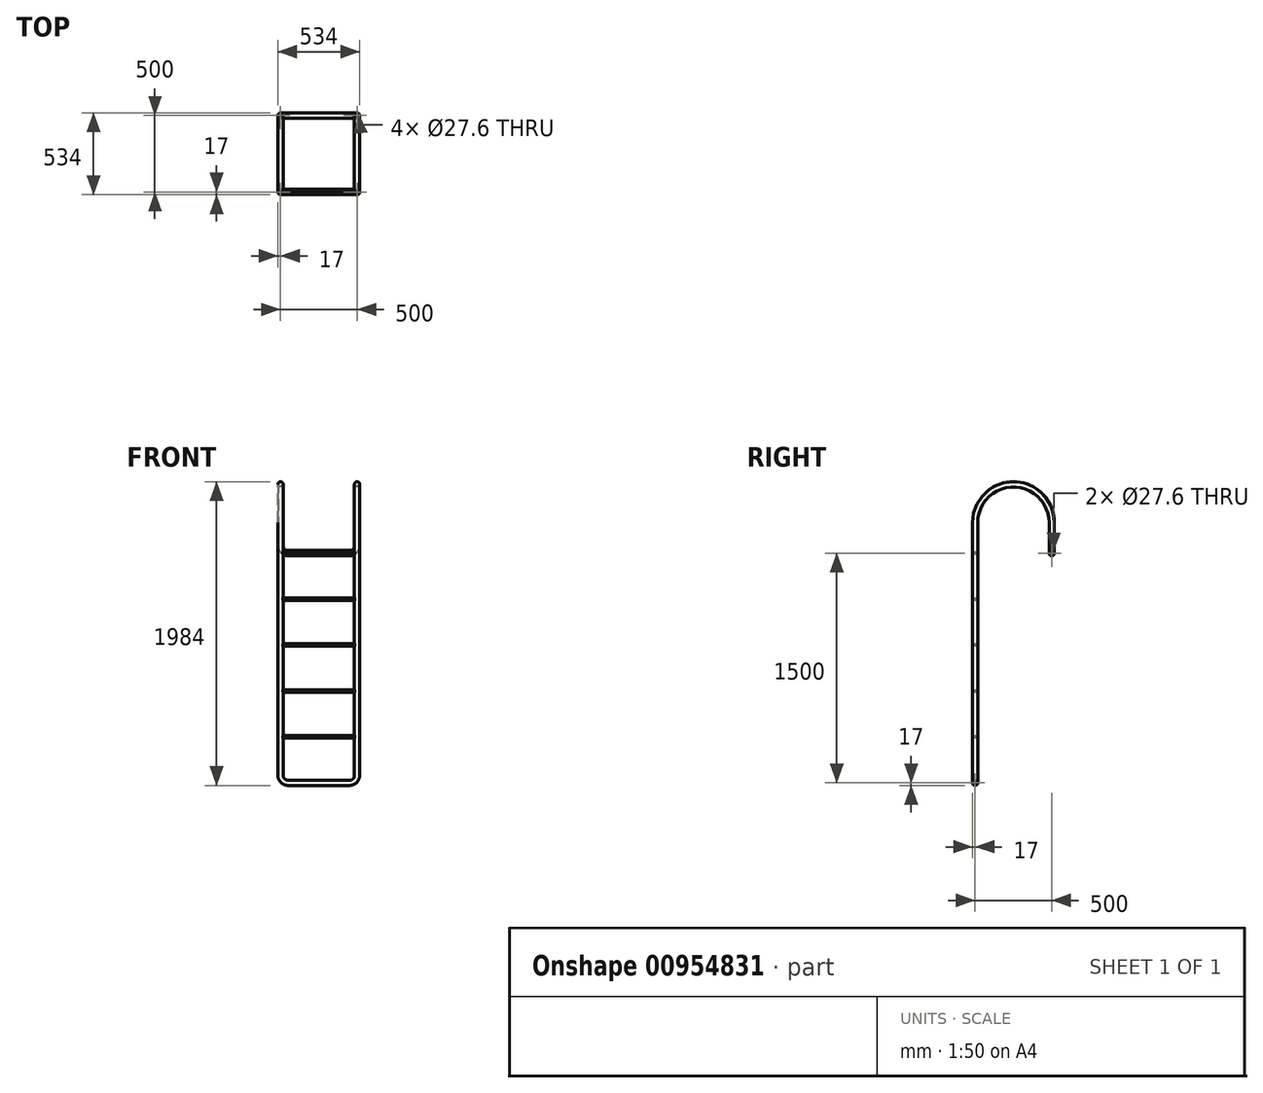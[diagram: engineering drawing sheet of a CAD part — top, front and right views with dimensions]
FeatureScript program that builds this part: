
annotation { "Feature Type Name" : "Feature", "Feature Type Description" : "" }
export const myFeature = defineFeature(function(context is Context, id is Id, definition is map)
    precondition{}
    {
        {
            var Q0;
            Q0=qCreatedBy(makeId("Right.planeOp"),FACE);
            cPlane(context, id + "F0", {"entities" : qUnion([Q0]), "cplaneType" : CPlaneType.OFFSET, "offset" : 250 * mm, "width" : 150 * mm, "height" : 150 * mm});
        }
        {
            var Q0;
            Q0=qCreatedBy(id+"F0.planeOp",FACE);
            var sketch = newSketch(context, id + "F1", { "sketchPlane" : qUnion([Q0])});
            skLineSegment(sketch, "E0", {"start": v(0, 0) * mm, "end": v(0, 100) * mm});
            skArc(sketch, "E1", {"start": v(0, 100) * mm, "mid": v(-250, 350) * mm, "end": v(-500, 100) * mm});
            skLineSegment(sketch, "E2", {"start": v(-500, 100) * mm, "end": v(-500, -1500) * mm});
            skSolve(sketch);
        }
        {
            var Q0;
            Q0=qCreatedBy(makeId("Top.planeOp"),FACE);
            var sketch = newSketch(context, id + "F2", { "sketchPlane" : qUnion([Q0])});
            skCircle(sketch, "E3", {"center": v(250, 0) * mm, "radius": 17 * mm});
            skCircle(sketch, "E4.0", {"center": v(250, 0) * mm, "radius": 13.8 * mm});
            skSolve(sketch);
        }
        {
            var Q0;
            Q0 = qSketchRegion(id + "F2", true);
            var Q1;
            Q1 = qConstructionFilter(qBodyType(qCreatedBy(id + "F1" ,EDGE), BodyType.WIRE), ConstructionObject.NO);
            sweep(context, id + "F3", {"profiles" : qUnion([Q0]), "path" : qUnion([Q1])});
        }
        {
            var Q0;
            Q0=makeQuery(id+"F3.opSweep","SWEPT_BODY",BODY,{"disambiguationData":[OSD([sQuery(id+"F1.wireOp",EDGE,"E2"),sQuery(id+"F2.wireOp",EDGE,"E3"),sQuery(id+"F2.wireOp",EDGE,"E4.0")])]});
            var Q1;
            Q1=qCreatedBy(makeId("Right.planeOp"),FACE);
            mirror(context, id + "F4", {"entities" : qUnion([Q0]), "mirrorPlane" : qUnion([Q1])});
        }
        {
            var Q0;
            Q0=qCreatedBy(makeId("Front.planeOp"),FACE);
            var sketch = newSketch(context, id + "F5", { "sketchPlane" : qUnion([Q0])});
            skLineSegment(sketch, "E5", {"start": v(250, 0) * mm, "end": v(250, -50) * mm});
            skLineSegment(sketch, "E6", {"start": v(200, -100) * mm, "end": v(-200, -100) * mm});
            skLineSegment(sketch, "E7", {"start": v(-250, -50) * mm, "end": v(-250, 0) * mm});
            skPoint(sketch, "E8.visualSharp", {"position": v(-250, -100) * mm});
            skArc(sketch, "E8.filletArc", {"start": v(-250, -50) * mm, "mid": v(-235.36, -85.36) * mm, "end": v(-200, -100) * mm});
            skPoint(sketch, "E9.visualSharp", {"position": v(250, -100) * mm});
            skArc(sketch, "E9.filletArc", {"start": v(200, -100) * mm, "mid": v(235.36, -85.36) * mm, "end": v(250, -50) * mm});
            skSolve(sketch);
        }
        {
            var Q0;
            Q0 = qSketchRegion(id + "F2", true);
            var Q1;
            Q1 = qConstructionFilter(qBodyType(qCreatedBy(id + "F5" ,EDGE), BodyType.WIRE), ConstructionObject.NO);
            sweep(context, id + "F6", {"operationType" : NewBodyOperationType.ADD, "profiles" : qUnion([Q0]), "path" : qUnion([Q1])});
        }
        {
            var Q0;
            Q0=qCreatedBy(makeId("Front.planeOp"),FACE);
            cPlane(context, id + "F7", {"entities" : qUnion([Q0]), "cplaneType" : CPlaneType.OFFSET, "offset" : 500 * mm, "width" : 150 * mm, "height" : 150 * mm});
        }
        {
            var Q0;
            Q0=qCreatedBy(id+"F7.planeOp",FACE);
            var sketch = newSketch(context, id + "F8", { "sketchPlane" : qUnion([Q0])});
            skLineSegment(sketch, "E10", {"start": v(250, -1500) * mm, "end": v(250, -1550) * mm});
            skLineSegment(sketch, "E11", {"start": v(200, -1600) * mm, "end": v(-200, -1600) * mm});
            skLineSegment(sketch, "E12", {"start": v(-250, -1550) * mm, "end": v(-250, -1500) * mm});
            skPoint(sketch, "E13.visualSharp", {"position": v(-250, -1600) * mm});
            skArc(sketch, "E13.filletArc", {"start": v(-250, -1550) * mm, "mid": v(-235.36, -1585.36) * mm, "end": v(-200, -1600) * mm});
            skPoint(sketch, "E14.visualSharp", {"position": v(250, -1600) * mm});
            skArc(sketch, "E14.filletArc", {"start": v(200, -1600) * mm, "mid": v(235.36, -1585.36) * mm, "end": v(250, -1550) * mm});
            skSolve(sketch);
        }
        {
            var Q0;
            Q0=makeQuery(id+"F3.opSweep","CAP_FACE",FACE,{"disambiguationData":[OSD([sQuery(id+"F1.wireOp",VERTEX,"E2.end"),sQuery(id+"F2.wireOp",EDGE,"E3"),sQuery(id+"F2.wireOp",EDGE,"E4.0")])],"isStart":false});
            var Q1;
            Q1 = qConstructionFilter(qBodyType(qCreatedBy(id + "F8" ,EDGE), BodyType.WIRE), ConstructionObject.NO);
            sweep(context, id + "F9", {"operationType" : NewBodyOperationType.ADD, "profiles" : qUnion([Q0]), "path" : qUnion([Q1])});
        }
        {
            var Q0;
            Q0=qCreatedBy(makeId("Right.planeOp"),FACE);
            var sketch = newSketch(context, id + "F10", { "sketchPlane" : qUnion([Q0])});
            skCircle(sketch, "E15", {"center": v(-500, -1300) * mm, "radius": 8 * mm});
            skCircle(sketch, "E16.0.1.0", {"center": v(-500, -1000) * mm, "radius": 8 * mm});
            skCircle(sketch, "E16.0.2.0", {"center": v(-500, -700) * mm, "radius": 8 * mm});
            skCircle(sketch, "E16.0.3.0", {"center": v(-500, -400) * mm, "radius": 8 * mm});
            skCircle(sketch, "E16.0.4.0", {"center": v(-500, -100) * mm, "radius": 8 * mm});
            skLineSegment(sketch, "E16.direction1", {"start": v(-500, -1300) * mm, "end": v(-475, -1300) * mm, "construction": true});
            skLineSegment(sketch, "E16.direction2", {"start": v(-500, -1300) * mm, "end": v(-500, -1000) * mm, "construction": true});
            skSolve(sketch);
        }
        {
            var Q0;
            Q0 = qSketchRegion(id + "F10", true);
            extrude(context, id + "F11", {"entities" : qUnion([Q0]), "operationType" : NewBodyOperationType.ADD, "endBound" : BoundingType.UP_TO_NEXT, "depth" : 25 * mm, "offsetDistance" : 25 * mm, "hasSecondDirection" : true, "secondDirectionBound" : BoundingType.UP_TO_NEXT, "secondDirectionOppositeDirection" : true, "secondDirectionDepth" : 25 * mm});
        }
    });
